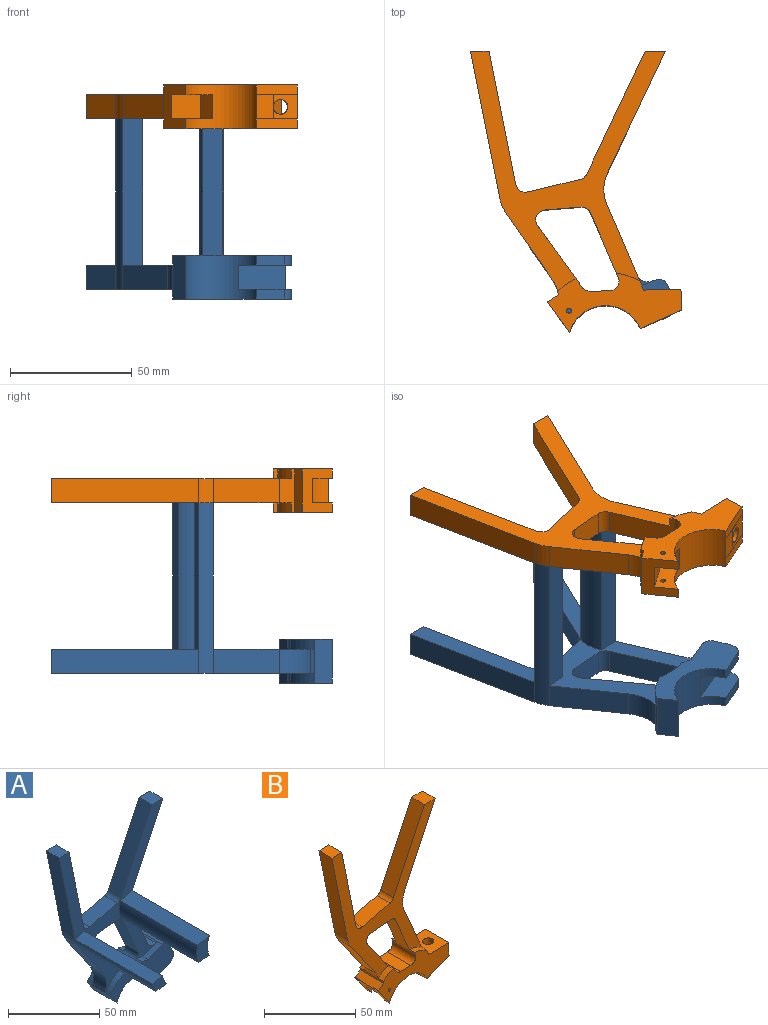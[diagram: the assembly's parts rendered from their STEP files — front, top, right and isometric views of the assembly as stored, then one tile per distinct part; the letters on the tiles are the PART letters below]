
ASSEMBLY  parts=2 mates=1
PART A: 52 faces, bbox 84.2x74x115.4 mm
  f0: plane 11.48x4.95mm, normal (0.4,0,-0.92), area 50mm2, adj f19,f31,f37,f42
  f1: plane 18x6.43mm, normal (0.92,0,0.4), area 76mm2, adj f31,f36,f37,f38,f39,f41,f42,f43
  f2: plane 18x11.08mm, normal (-0.4,0,0.92), area 106.5mm2, adj f29,f30,f31,f32,f34,f36,f40,f41
  f3: plane 28.51x12.28mm, normal (0.92,0,0.4), area 310.4mm2, adj f4,f29,f30,f40
  f4: cylinder r=16mm len=70mm, axis (0,1,0), area 952.5mm2, adj f3,f5,f30,f48,f50,f51
  f5: plane 49.9x23.72mm, normal (0.9,0,-0.43), area 552.6mm2, adj f4,f6,f29,f30
  f6: plane 10x8.3mm, normal (0,0,1), area 83mm2, adj f5,f7,f29,f30
  f7: plane 50.43x23.97mm, normal (-0.9,0,0.43), area 558.3mm2, adj f6,f8,f29,f30
  f8: cylinder r=4mm len=10mm, axis (0,1,0), area 35.7mm2, adj f7,f9,f29,f30
  f9: plane 21.62x10mm, normal (-0.23,0,0.97), area 222.4mm2, adj f8,f10,f29,f30
  f10: cylinder r=4mm len=10mm, axis (0,1,0), area 64.4mm2, adj f9,f11,f29,f30
  f11: plane 54.68x10.92mm, normal (0.98,0,0.2), area 557.6mm2, adj f10,f12,f29,f30
  f12: plane 10x7.65mm, normal (0,0,1), area 76.5mm2, adj f11,f13,f29,f30
  f13: plane 60.51x12.08mm, normal (-0.98,0,-0.2), area 617.1mm2, adj f12,f14,f29,f30
  f14: cylinder r=16mm len=70mm, axis (0,1,0), area 459.4mm2, adj f13,f15,f30,f45,f46,f47
  f15: plane 27.07x18.81mm, normal (-0.82,0,-0.57), area 329.6mm2, adj f14,f16,f29,f30
  f16: cylinder r=16mm len=12.98mm, axis (0,1,0), area 136.1mm2, adj f15,f17,f29,f30
  f17: plane 10x1.6mm, normal (-0.97,0,0.24), area 16.5mm2, adj f16,f18,f29,f30
  f18: plane 18x7.28mm, normal (-0.81,0,-0.59), area 161.5mm2, adj f17,f19,f31,f33,f35,f36
  f19: cylinder r=15.5mm len=29.05mm, axis (0,1,0), area 570.9mm2, adj f0,f18,f20,f31,f36,f37,f38,f39
  f20: plane 11.48x4.95mm, normal (0.4,0,-0.92), area 50mm2, adj f19,f36,f39,f43
  f21: cylinder r=4mm len=18mm, axis (0,1,0), area 103.7mm2, adj f22,f28,f29,f30,f31,f32,f34,f36
  f22: plane 18x7.93mm, normal (-0.02,0,1), area 142.8mm2, adj f21,f23,f31,f36
  f23: cylinder r=4mm len=18mm, axis (0,1,0), area 53.6mm2, adj f22,f24,f29,f30,f31,f33,f35,f36
  f24: plane 25.37x18.31mm, normal (0.81,0,0.59), area 312.8mm2, adj f23,f25,f29,f30
  f25: cylinder r=4mm len=10mm, axis (0,1,0), area 84.6mm2, adj f24,f26,f29,f30
  f26: plane 14.86x10mm, normal (0.08,0,-1), area 149.1mm2, adj f25,f27,f29,f30
  f27: cylinder r=4mm len=10mm, axis (0,1,0), area 49.8mm2, adj f26,f28,f29,f30
  f28: plane 26.42x11.38mm, normal (-0.92,0,-0.4), area 287.6mm2, adj f21,f27,f29,f30
  f29: plane 108.16x80mm, normal (0,-1,0), area 1782.5mm2, adj f2,f3,f5,f6,f7,f8,f9,f10
  f30: plane 108.16x80mm, normal (0,1,0), area 1944.3mm2, adj f2,f3,f4,f5,f6,f7,f8,f9
  f31: plane 48.8x21.93mm, normal (0,1,0), area 508.7mm2, adj f0,f1,f2,f18,f19,f21,f22,f23
  f32: cylinder r=23.3mm len=4.81mm, axis (0,1,0), area 20.2mm2, adj f2,f21,f30,f31
  f33: cylinder r=23.3mm len=11.91mm, axis (0,1,0), area 63.4mm2, adj f18,f23,f30,f31
  f34: cylinder r=23.3mm len=4.81mm, axis (0,1,0), area 20.2mm2, adj f2,f21,f29,f36
  f35: cylinder r=23.3mm len=11.91mm, axis (0,1,0), area 63.4mm2, adj f18,f23,f29,f36
  f36: plane 48.8x21.93mm, normal (0,-1,0), area 508.7mm2, adj f1,f2,f18,f19,f20,f21,f22,f23
  f37: plane 21.82x16.11mm, normal (0,-1,0), area 181.2mm2, adj f0,f1,f19,f38,f42
  f38: plane 19.43x10mm, normal (0.4,0,-0.92), area 211.6mm2, adj f1,f19,f37,f39
  f39: plane 21.82x16.11mm, normal (0,1,0), area 181.2mm2, adj f1,f19,f20,f38,f43
  f40: cylinder r=5mm len=10mm, axis (0,1,0), area 78.5mm2, adj f2,f3,f29,f30
  f41: cylinder r=4mm len=18mm, axis (0,1,0), area 113.1mm2, adj f1,f2,f31,f36
  f42: cylinder r=5mm len=6.57mm, axis (0,1,0), area 31.4mm2, adj f0,f1,f31,f37
  f43: cylinder r=5mm len=6.57mm, axis (0,1,0), area 31.4mm2, adj f1,f20,f36,f39
  f44: cylinder r=33.27mm len=60mm, axis (0,1,0), area 473.6mm2, adj f29,f45,f46,f47
  f45: plane 60x7.55mm, normal (-0.23,0,0.97), area 465.9mm2, adj f14,f29,f44,f47
  f46: plane 60x8.36mm, normal (0.08,0,-1), area 503.2mm2, adj f14,f29,f44,f47
  f47: plane 10.91x7.81mm, normal (0,-1,0), area 56.1mm2, adj f14,f44,f45,f46
  f48: plane 60x9.24mm, normal (-0.23,0,0.97), area 570.1mm2, adj f4,f29,f49,f51
  f49: cylinder r=15.57mm len=60mm, axis (0,1,0), area 718.7mm2, adj f29,f48,f50,f51
  f50: plane 60x8.31mm, normal (0.08,0,-1), area 500.5mm2, adj f4,f29,f49,f51
  f51: plane 13.88x10.06mm, normal (0,-1,0), area 105.7mm2, adj f4,f48,f49,f50
PART B: 50 faces, bbox 86.6x18x115.4 mm
  f0: plane 18x12.43mm, normal (-0.81,0,-0.59), area 175.8mm2, adj f1,f21,f33,f36,f38,f42,f44,f45
  f1: cylinder r=15.5mm len=29.05mm, axis (0,1,0), area 521.4mm2, adj f0,f22,f33,f37,f41,f42,f44,f45
  f2: plane 98.47x80mm, normal (0,-1,0), area 1825.1mm2, adj f7,f8,f9,f10,f11,f12,f13,f14
  f3: plane 16.89x7.58mm, normal (0,-1,0), area 1mm2, adj f22,f23,f41
  f4: plane 98.47x80mm, normal (0,1,0), area 1825.1mm2, adj f7,f8,f9,f10,f11,f12,f13,f14
  f5: plane 16.89x7.58mm, normal (0,1,0), area 1mm2, adj f22,f23,f37
  f6: plane 18x15.33mm, normal (-0.02,0,1), area 247mm2, adj f7,f32,f33,f42,f43
  f7: plane 34.98x18mm, normal (0.92,0,0.4), area 413.5mm2, adj f2,f4,f6,f8,f33,f34,f39,f42
  f8: cylinder r=16mm len=13.2mm, axis (0,1,0), area 136.1mm2, adj f2,f4,f7,f9
  f9: plane 49.9x23.72mm, normal (0.9,0,-0.43), area 552.6mm2, adj f2,f4,f8,f10
  f10: plane 10x8.3mm, normal (0,0,1), area 83mm2, adj f2,f4,f9,f11
  f11: plane 50.43x23.97mm, normal (-0.9,0,0.43), area 558.3mm2, adj f2,f4,f10,f12
  f12: cylinder r=4mm len=10mm, axis (0,1,0), area 35.7mm2, adj f2,f4,f11,f13
  f13: plane 21.62x10mm, normal (-0.23,0,0.97), area 222.4mm2, adj f2,f4,f12,f14
  f14: cylinder r=4mm len=10mm, axis (0,1,0), area 64.4mm2, adj f2,f4,f13,f15
  f15: plane 54.68x10.92mm, normal (0.98,0,0.2), area 557.6mm2, adj f2,f4,f14,f16
  f16: plane 10x7.65mm, normal (0,0,1), area 76.5mm2, adj f2,f4,f15,f17
  f17: plane 60.51x12.08mm, normal (-0.98,0,-0.2), area 617.1mm2, adj f2,f4,f16,f18
  f18: cylinder r=16mm len=10mm, axis (0,1,0), area 65.6mm2, adj f2,f4,f17,f19
  f19: plane 27.07x18.81mm, normal (-0.82,0,-0.57), area 329.6mm2, adj f2,f4,f18,f20
  f20: cylinder r=16mm len=18mm, axis (0,1,0), area 80.4mm2, adj f2,f4,f19,f21,f33,f35,f40,f42
  f21: plane 18x4.34mm, normal (-0.59,0,0.81), area 93.7mm2, adj f0,f20,f33,f36,f38,f42
  f22: plane 10x6.89mm, normal (0.4,0,-0.92), area 75mm2, adj f1,f3,f5,f23
  f23: plane 10x10mm, normal (0.42,0,-0.91), area 78.4mm2, adj f3,f5,f22,f32,f43
  f24: cylinder r=4mm len=18mm, axis (0,1,0), area 140.8mm2, adj f25,f31,f33,f42
  f25: plane 18x7.93mm, normal (-0.02,0,1), area 142.8mm2, adj f24,f26,f33,f42
  f26: cylinder r=4mm len=18mm, axis (0,1,0), area 69.7mm2, adj f25,f27,f33,f42
  f27: plane 25.37x18.31mm, normal (0.81,0,0.59), area 347.1mm2, adj f2,f4,f26,f28,f33,f35,f40,f42
  f28: cylinder r=4mm len=10mm, axis (0,1,0), area 84.6mm2, adj f2,f4,f27,f29
  f29: plane 14.86x10mm, normal (0.08,0,-1), area 149.1mm2, adj f2,f4,f28,f30
  f30: cylinder r=4mm len=10mm, axis (0,1,0), area 49.8mm2, adj f2,f4,f29,f31
  f31: plane 26.42x18mm, normal (-0.92,0,-0.4), area 302.4mm2, adj f2,f4,f24,f30,f33,f34,f39,f42
  f32: plane 18x8.54mm, normal (1,0,0.02), area 153.7mm2, adj f6,f23,f33,f37,f41,f42
  f33: plane 54.9x24.32mm, normal (0,1,0), area 629.2mm2, adj f0,f1,f6,f7,f20,f21,f24,f25
  f34: cylinder r=29.22mm len=9.56mm, axis (0,1,0), area 40.6mm2, adj f4,f7,f31,f33
  f35: cylinder r=29.22mm len=7.58mm, axis (0,1,0), area 36.5mm2, adj f4,f20,f27,f33
  f36: cylinder r=6.76mm len=4mm, axis (0,1,0), area 1.2mm2, adj f0,f21,f33
  f37: plane 16.89x7.58mm, normal (0.41,0,-0.91), area 74mm2, adj f1,f5,f32,f33
  f38: cylinder r=6.76mm len=4mm, axis (0,1,0), area 1.2mm2, adj f0,f21,f42
  f39: cylinder r=29.22mm len=9.56mm, axis (0,1,0), area 40.6mm2, adj f2,f7,f31,f42
  f40: cylinder r=29.22mm len=7.58mm, axis (0,1,0), area 36.5mm2, adj f2,f20,f27,f42
  f41: plane 16.89x7.58mm, normal (0.41,0,-0.91), area 74mm2, adj f1,f3,f32,f42
  f42: plane 54.9x24.32mm, normal (0,-1,0), area 629.2mm2, adj f0,f1,f6,f7,f20,f21,f24,f25
  f43: cylinder r=3.04mm len=13.06mm, axis (-0.02,0,1), area 221.4mm2, adj f6,f23
  f44: plane 16.89x16.81mm, normal (0,-1,0), area 111.2mm2, adj f0,f1,f46,f47,f49
  f45: plane 16.89x16.81mm, normal (0,1,0), area 111.2mm2, adj f0,f1,f46,f47,f48
  f46: plane 12.16x10mm, normal (0.59,0,-0.81), area 150mm2, adj f0,f44,f45,f47
  f47: plane 10x6.44mm, normal (-0.81,0,-0.59), area 79.4mm2, adj f1,f44,f45,f46
  f48: cylinder r=1mm len=4mm, axis (0,-1,0), area 25.1mm2, adj f42,f45
  f49: cylinder r=1mm len=4mm, axis (0,-1,0), area 25.1mm2, adj f33,f44
PLACE A rot(axis=(-1,0,0),90deg) t=(-35.8,-11.76,-52.02)mm
PLACE B rot(axis=(-1,0,0),90deg) t=(-35.8,-11.76,17.98)mm
MATE fastened B.f4 <-> A.f51  axis (0,0,-1) through (-19.52,-7.66,17.98)mm
